# Revit family: SM772
name_source: partatom
category: Generic Models
units: mm (PartAtom-declared; Revit-internal decimal feet)

## family parameters
Always vertical = No
Can host rebar = No
Cut with Voids When Loaded = No
Maintain Annotation Orientation = No
OmniClass Number = 23.50.70.00
OmniClass Title = Loading Dock Equipment
Part Type = Normal
Room Calculation Point = No
Round Connector Dimension = Use Diameter
Shared = No
Work Plane-Based = Yes

## types (1)
- SM772
    Construction Details = http://www.OVERHEADDOOR.COM
    Default Elevation = 4' - 0"
    Expected Lifespan (Years) = 0
    Maintenance Schedule (Months) = 0
    Manufacturer Website = http://www.OVERHEADDOOR.COM
    Material = Plastic - Vinyl - Blue
    Pad Width = 0' - 8"
    Product Data = http://www.OVERHEADDOOR.COM
    Revision = R1_07-2011
    Sales Information = http://www.OVERHEADDOOR.COM
    Unit Depth = 1' - 4"
    Warranty Duration (Years) = 0

## geometry (parser evidence)
native form markers: Blend x42, Sweep x6
no freeform markers — native parametric forms only
